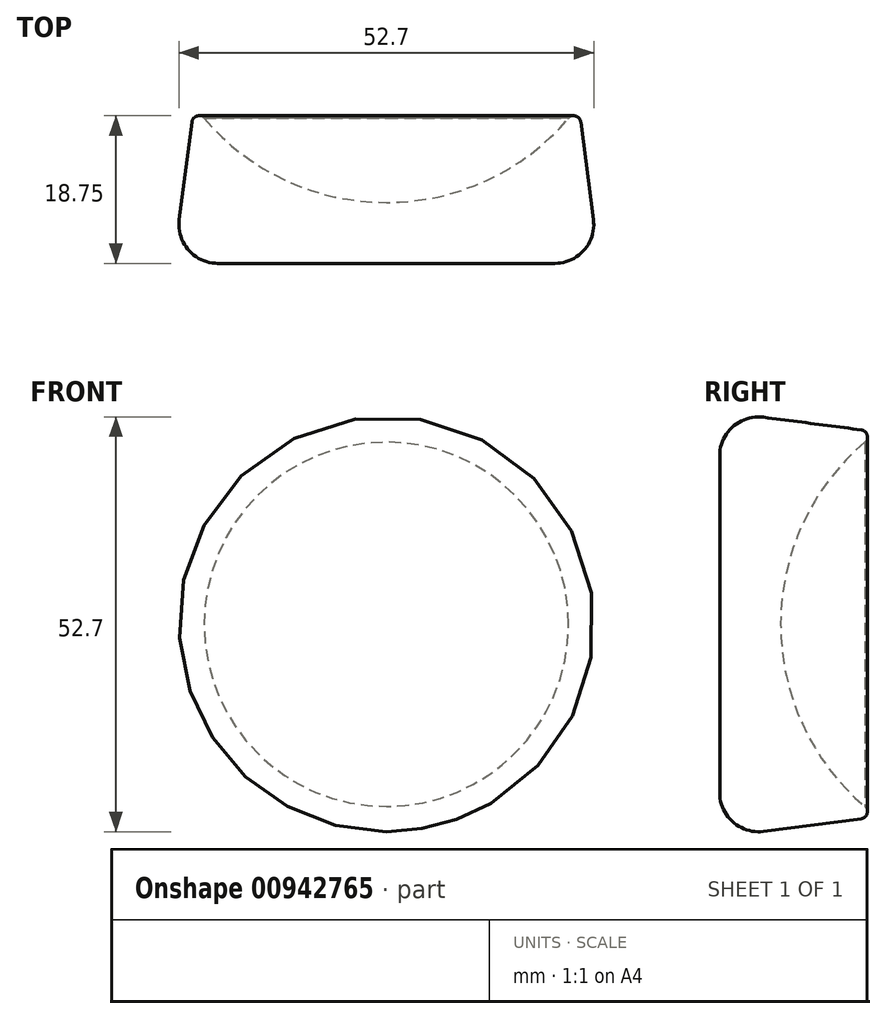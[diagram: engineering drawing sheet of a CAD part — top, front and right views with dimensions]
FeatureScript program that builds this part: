
annotation { "Feature Type Name" : "Feature", "Feature Type Description" : "" }
export const myFeature = defineFeature(function(context is Context, id is Id, definition is map)
    precondition{}
    {
        {
            var Q0;
            Q0=qCreatedBy(makeId("Front.planeOp"),FACE);
            var sketch = newSketch(context, id + "F0", { "sketchPlane" : qUnion([Q0])});
            skLineSegment(sketch, "E0", {"start": v(0, 29.29) * mm, "end": v(0, 29.29) * mm});
            skLineSegment(sketch, "E1", {"start": v(0, 29.29) * mm, "end": v(0, -29.29) * mm});
            skLineSegment(sketch, "E2", {"start": v(0, -29.29) * mm, "end": v(0, -29.29) * mm});
            skArc(sketch, "E3", {"start": v(0, 29.29) * mm, "mid": v(-29.29, 0) * mm, "end": v(0, -29.29) * mm, "construction": true});
            skArc(sketch, "E4", {"start": v(0, -29.29) * mm, "mid": v(29.29, 0) * mm, "end": v(0, 29.29) * mm});
            skSolve(sketch);
        }
        {
            var Q0;
            Q0=sQuery(id+"F0.wireOp",EDGE,"E4");
            var Q1;
            Q1=sQuery(id+"F0.wireOp",EDGE,"E1");
            revolve(context, id + "F1", {"bodyType" : ToolBodyType.SURFACE, "surfaceOperationType" : NewSurfaceOperationType.NEW, "surfaceEntities" : qUnion([Q0]), "axis" : qUnion([Q1]), "revolveType" : RevolveType.FULL});
        }
        {
            var Q0;
            Q0=qCreatedBy(makeId("Front.planeOp"),FACE);
            var sketch = newSketch(context, id + "F2", { "sketchPlane" : qUnion([Q0])});
            skCircle(sketch, "E5", {"center": v(0, 0) * mm, "radius": 22.09 * mm});
            skSolve(sketch);
        }
        {
            var Q0;
            Q0=qCreatedBy(makeId("Front.planeOp"),FACE);
            cPlane(context, id + "F3", {"entities" : qUnion([Q0]), "cplaneType" : CPlaneType.OFFSET, "offset" : 38.1 * mm, "width" : 152.4 * mm, "height" : 152.4 * mm});
        }
        {
            var Q0;
            Q0=qCreatedBy(id+"F3.planeOp",FACE);
            var sketch = newSketch(context, id + "F4", { "sketchPlane" : qUnion([Q0])});
            skCircle(sketch, "E6", {"center": v(0, 0) * mm, "radius": 27.03 * mm});
            skSolve(sketch);
        }
        {
            var Q0;
            Q0=makeQuery(id+"F4.imprint","IMPRINT",FACE,{"disambiguationData":[TD([[makeQuery(id+"F4.imprint","IMPRINT",EDGE,{"derivedFrom":sQuery(id+"F4.wireOp",EDGE,"E6")}),1.0]])]});
            var Q1;
            Q1 = qSketchRegion(id + "F2", true);
            loft(context, id + "F5", {"sheetProfilesArray" : [{ "sheetProfileEntities" : qUnion([Q0]) }, { "sheetProfileEntities" : qUnion([Q1]) }]});
        }
        {
            var Q0;
            Q0=qCreatedBy(makeId("Front.planeOp"),FACE);
            var sketch = newSketch(context, id + "F6", { "sketchPlane" : qUnion([Q0])});
            skLineSegment(sketch, "E7", {"start": v(0, 30.37) * mm, "end": v(0, 30.37) * mm});
            skLineSegment(sketch, "E8", {"start": v(0, 30.37) * mm, "end": v(0, -30.37) * mm});
            skLineSegment(sketch, "E9", {"start": v(0, -30.37) * mm, "end": v(0, -30.37) * mm});
            skArc(sketch, "E10", {"start": v(0, 30.37) * mm, "mid": v(-30.37, 0) * mm, "end": v(0, -30.37) * mm, "construction": true});
            skArc(sketch, "E11", {"start": v(0, -30.37) * mm, "mid": v(30.37, 0) * mm, "end": v(0, 30.37) * mm});
            skSolve(sketch);
        }
        {
            var Q0;
            Q0 = qSketchRegion(id + "F6", true);
            var Q1;
            Q1=sQuery(id+"F0.wireOp",EDGE,"E1");
            revolve(context, id + "F7", {"surfaceOperationType" : NewSurfaceOperationType.NEW, "entities" : qUnion([Q0]), "axis" : qUnion([Q1]), "revolveType" : RevolveType.FULL});
        }
        {
            var Q0;
            Q0=makeQuery(id+"F7.opRevolve","SWEPT_BODY",BODY,{"disambiguationData":[OSD([sQuery(id+"F6.wireOp",EDGE,"E8"),sQuery(id+"F6.wireOp",EDGE,"E11")])]});
            var Q1;
            Q1=makeQuery(id+"F5.opLoft","SWEPT_BODY",BODY,{"disambiguationData":[OSD([makeQuery(id+"F2.imprint","IMPRINT",FACE,{"disambiguationData":[TD([[makeQuery(id+"F2.imprint","IMPRINT",EDGE,{"derivedFrom":sQuery(id+"F2.wireOp",EDGE,"E5")}),1.0]])]}),makeQuery(id+"F4.imprint","IMPRINT",FACE,{"disambiguationData":[TD([[makeQuery(id+"F4.imprint","IMPRINT",EDGE,{"derivedFrom":sQuery(id+"F4.wireOp",EDGE,"E6")}),1.0]])]})])]});
            booleanBodies(context, id + "F8", {"operationType" : BooleanOperationType.SUBTRACTION, "tools" : qUnion([Q0]), "targets" : qUnion([Q1])});
        }
        {
            var Q0;
            Q0=makeQuery(id+"F8.opBoolean","INTERSECT",EDGE,{"derivedFrom":[makeQuery(id+"F5.opLoft","SWEPT_FACE",FACE,{"disambiguationData":[OSD([sQuery(id+"F2.wireOp",EDGE,"E5"),sQuery(id+"F4.wireOp",EDGE,"E6")])]}),makeQuery(id+"F7.opRevolve","SWEPT_FACE",FACE,{"disambiguationData":[OSD([sQuery(id+"F6.wireOp",EDGE,"E11")])]})]});
            fillet(context, id + "F9", {"entities" : qUnion([Q0]), "radius" : 0.89 * mm, "tangentPropagation" : true, "allowEdgeOverflow" : false});
        }
        {
            var Q0;
            Q0=makeQuery(id+"F5.opLoft","MID_CAP_EDGE",EDGE,{"disambiguationData":[OSD([sQuery(id+"F4.wireOp",EDGE,"E6")])],"capPos":0.0});
            fillet(context, id + "F10", {"entities" : qUnion([Q0]), "radius" : 4.93 * mm, "tangentPropagation" : true, "allowEdgeOverflow" : false});
        }
    });
